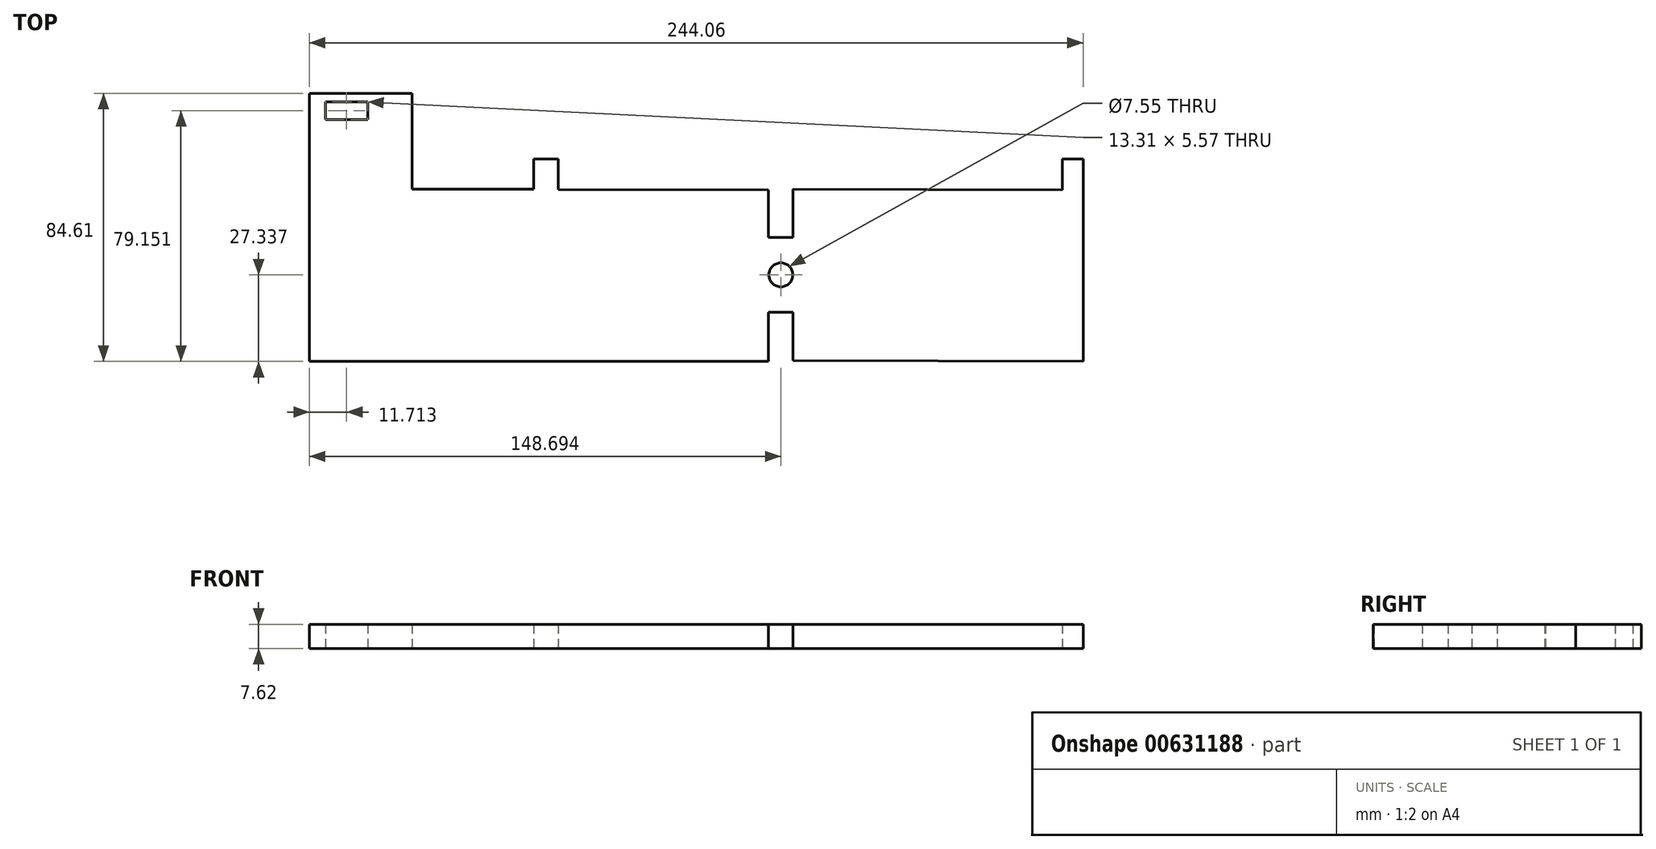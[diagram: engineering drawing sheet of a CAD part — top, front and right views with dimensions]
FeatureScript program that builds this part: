
annotation { "Feature Type Name" : "Feature", "Feature Type Description" : "" }
export const myFeature = defineFeature(function(context is Context, id is Id, definition is map)
    precondition{}
    {
        {
            var Q0;
            Q0=qCreatedBy(makeId("Top.planeOp"),FACE);
            var sketch = newSketch(context, id + "F0", { "sketchPlane" : qUnion([Q0])});
            skLineSegment(sketch, "E0", {"start": v(-125.92, -22.3) * mm, "end": v(18.85, -22.3) * mm});
            skLineSegment(sketch, "E1", {"start": v(18.85, -22.3) * mm, "end": v(18.85, -6.76) * mm});
            skLineSegment(sketch, "E2", {"start": v(18.85, -6.76) * mm, "end": v(26.62, -6.76) * mm});
            skLineSegment(sketch, "E3", {"start": v(26.62, -6.76) * mm, "end": v(26.62, -22.02) * mm});
            skLineSegment(sketch, "E4", {"start": v(26.62, -22.02) * mm, "end": v(118.14, -22.3) * mm});
            skLineSegment(sketch, "E5", {"start": v(118.14, -22.3) * mm, "end": v(118.14, 41.59) * mm});
            skLineSegment(sketch, "E6", {"start": v(118.14, 41.59) * mm, "end": v(111.53, 41.6) * mm});
            skLineSegment(sketch, "E7", {"start": v(26.62, 32.07) * mm, "end": v(111.5, 31.8) * mm});
            skLineSegment(sketch, "E8", {"start": v(26.62, 32.07) * mm, "end": v(26.62, 16.84) * mm});
            skLineSegment(sketch, "E9", {"start": v(26.62, 16.84) * mm, "end": v(18.85, 16.84) * mm});
            skLineSegment(sketch, "E10", {"start": v(18.85, 16.84) * mm, "end": v(18.85, 31.8) * mm});
            skLineSegment(sketch, "E11", {"start": v(111.53, 41.6) * mm, "end": v(111.5, 31.8) * mm});
            skLineSegment(sketch, "E12", {"start": v(18.85, 31.8) * mm, "end": v(-47.43, 32.01) * mm});
            skLineSegment(sketch, "E13", {"start": v(-47.43, 32.01) * mm, "end": v(-47.43, 41.6) * mm});
            skLineSegment(sketch, "E14", {"start": v(-47.43, 41.6) * mm, "end": v(-55.22, 41.6) * mm});
            skLineSegment(sketch, "E15", {"start": v(-55.22, 41.6) * mm, "end": v(-55.22, 32.03) * mm});
            skLineSegment(sketch, "E16", {"start": v(-55.22, 32.03) * mm, "end": v(-93.54, 32.03) * mm});
            skLineSegment(sketch, "E17", {"start": v(-93.54, 32.03) * mm, "end": v(-93.54, 62.3) * mm});
            skLineSegment(sketch, "E18", {"start": v(-125.92, -22.3) * mm, "end": v(-125.92, 62.3) * mm});
            skLineSegment(sketch, "E19", {"start": v(-125.92, 62.3) * mm, "end": v(-93.54, 62.3) * mm});
            skLineSegment(sketch, "E20", {"start": v(-120.86, 54.07) * mm, "end": v(-120.86, 59.63) * mm});
            skLineSegment(sketch, "E21", {"start": v(-120.86, 59.63) * mm, "end": v(-107.55, 59.63) * mm});
            skLineSegment(sketch, "E22", {"start": v(-107.55, 59.63) * mm, "end": v(-107.55, 54.07) * mm});
            skLineSegment(sketch, "E23", {"start": v(-107.55, 54.07) * mm, "end": v(-120.86, 54.07) * mm});
            skCircle(sketch, "E24", {"center": v(22.77, 5.04) * mm, "radius": 3.78 * mm});
            skSolve(sketch);
        }
        {
            var Q0;
            Q0 = qSketchRegion(id + "F0", true);
            extrude(context, id + "F1", {"entities" : qUnion([Q0]), "depth" : 7.62 * mm, "offsetDistance" : 25.4 * mm});
        }
    });
